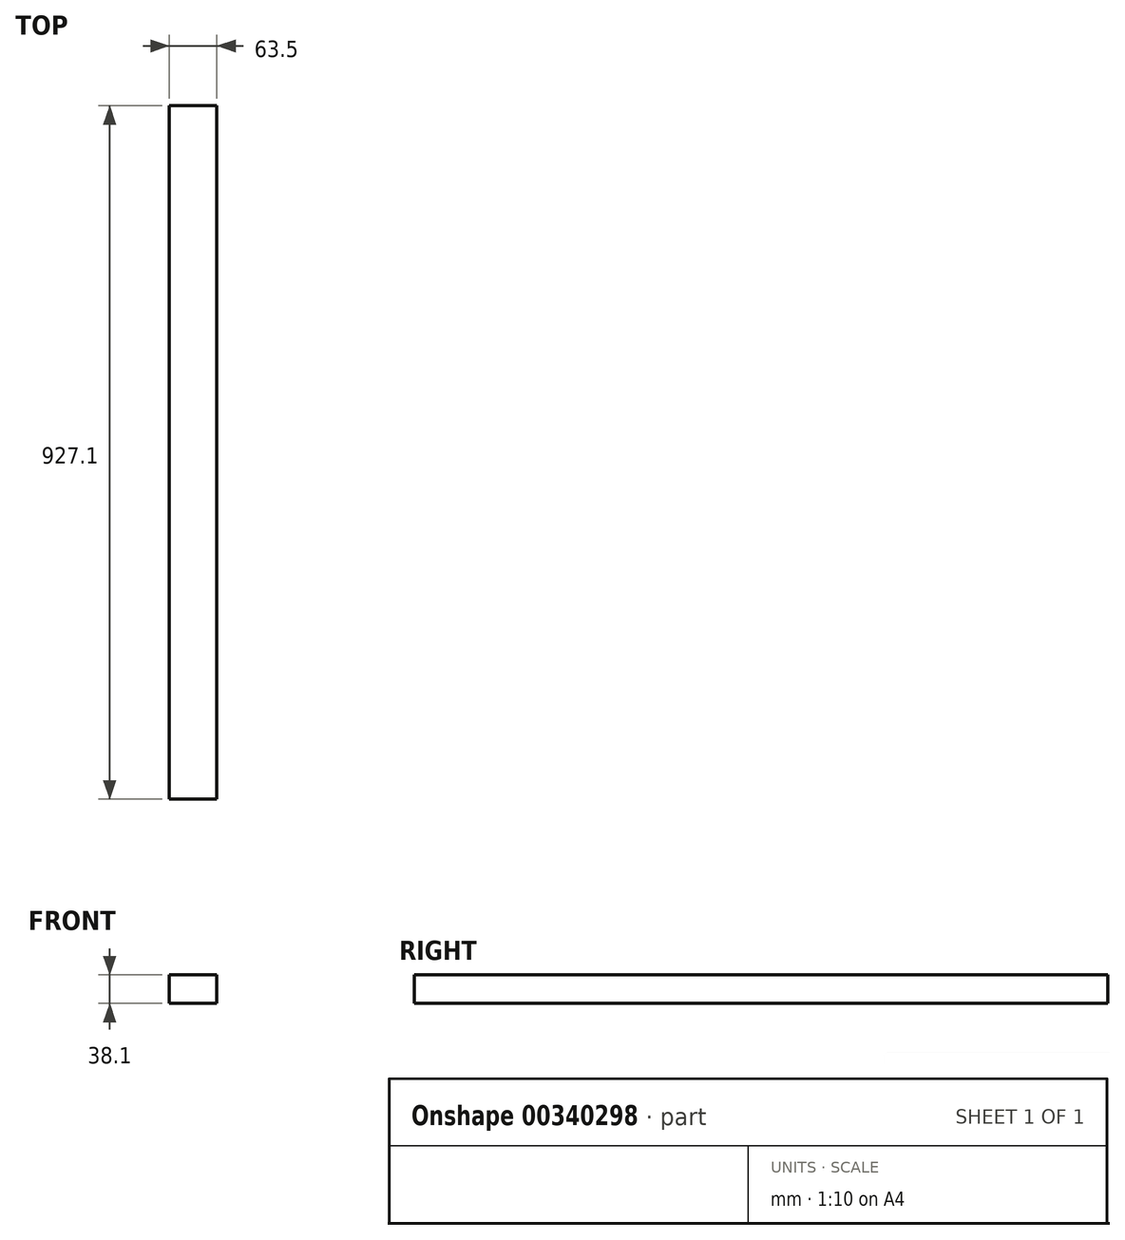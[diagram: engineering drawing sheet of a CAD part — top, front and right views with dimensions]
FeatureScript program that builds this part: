
annotation { "Feature Type Name" : "Feature", "Feature Type Description" : "" }
export const myFeature = defineFeature(function(context is Context, id is Id, definition is map)
    precondition{}
    {
        {
            var Q0;
            Q0=qCreatedBy(makeId("Front.planeOp"),FACE);
            var sketch = newSketch(context, id + "F0", { "sketchPlane" : qUnion([Q0])});
            skLineSegment(sketch, "E0.bottom", {"start": v(35.64, -16.66) * mm, "end": v(-27.86, -16.66) * mm});
            skLineSegment(sketch, "E0.top", {"start": v(35.64, 21.44) * mm, "end": v(-27.86, 21.44) * mm});
            skLineSegment(sketch, "E0.left", {"start": v(35.64, -16.66) * mm, "end": v(35.64, 21.44) * mm});
            skLineSegment(sketch, "E0.right", {"start": v(-27.86, -16.66) * mm, "end": v(-27.86, 21.44) * mm});
            skPoint(sketch, "E0.middle", {"position": v(3.9, 2.4) * mm});
            skSolve(sketch);
        }
        {
            var Q0;
            Q0=qSketchRegion(id+"F0",true);
            extrude(context, id + "F1", {"entities" : qUnion([Q0]), "depth" : 927.1 * mm});
        }
    });
